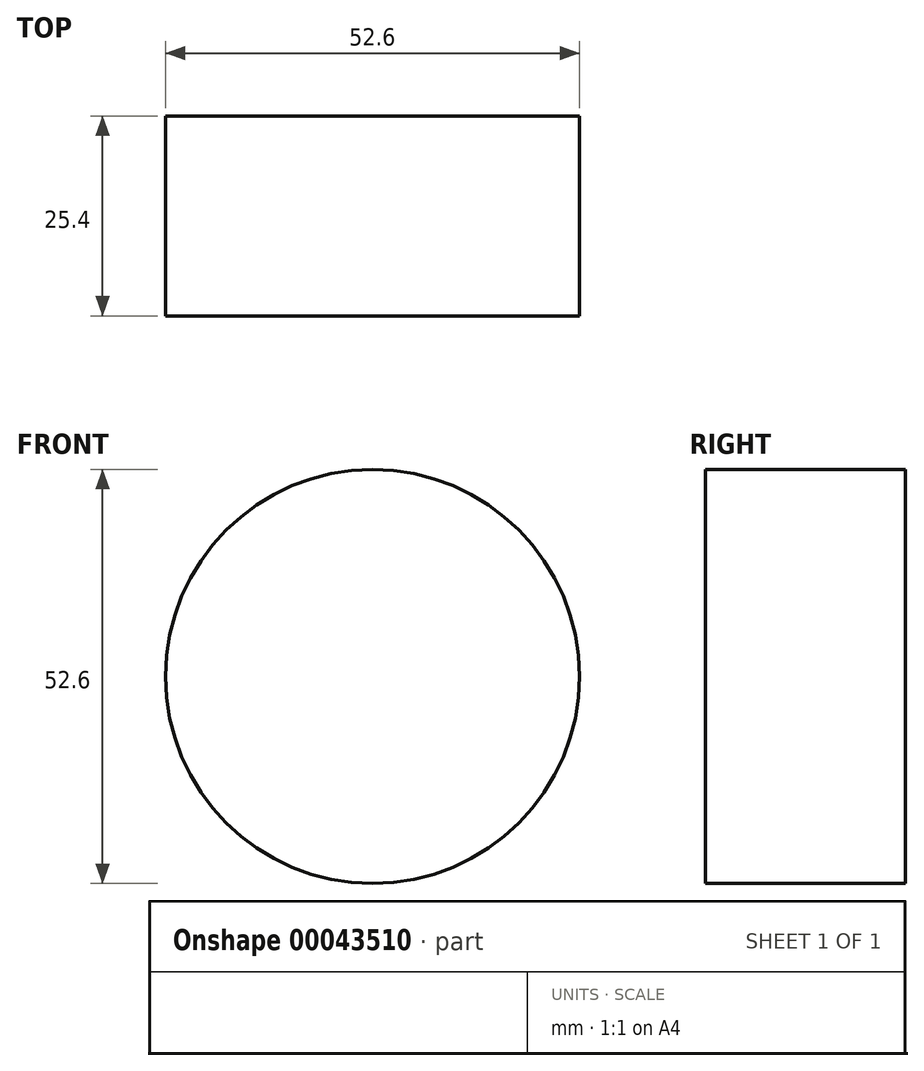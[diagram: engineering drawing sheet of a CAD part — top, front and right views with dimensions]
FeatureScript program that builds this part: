
annotation { "Feature Type Name" : "Feature", "Feature Type Description" : "" }
export const myFeature = defineFeature(function(context is Context, id is Id, definition is map)
    precondition{}
    {
        {
            var Q0;
            Q0=qCreatedBy(makeId("Front.planeOp"),FACE);
            var sketch = newSketch(context, id + "F0", { "sketchPlane" : qUnion([Q0])});
            skCircle(sketch, "E0", {"center": v(0, 0) * mm, "radius": 26.3 * mm});
            skSolve(sketch);
        }
        {
            var Q0;
            Q0 = qSketchRegion(id + "F0", true);
            extrude(context, id + "F1", {"entities" : qUnion([Q0]), "depth" : 25.4 * mm});
        }
    });
